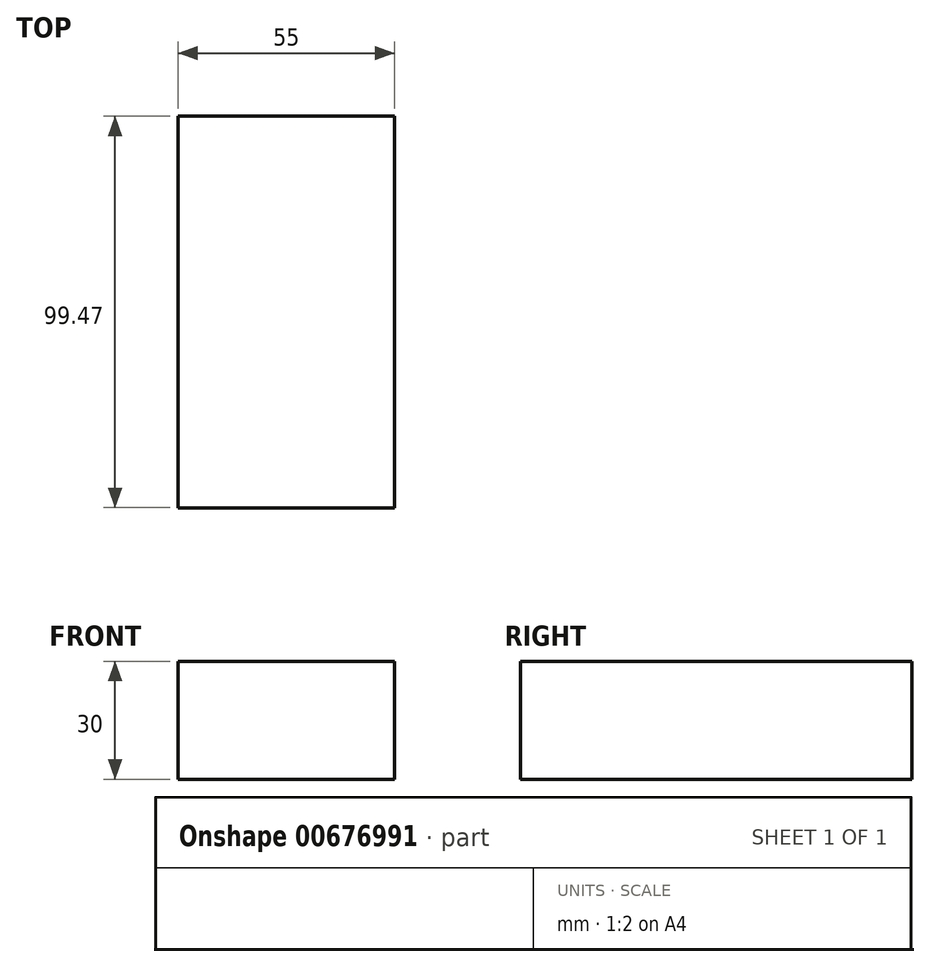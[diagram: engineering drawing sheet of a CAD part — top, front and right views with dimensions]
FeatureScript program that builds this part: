
annotation { "Feature Type Name" : "Feature", "Feature Type Description" : "" }
export const myFeature = defineFeature(function(context is Context, id is Id, definition is map)
    precondition{}
    {
        {
            var Q0;
            Q0=qCreatedBy(makeId("Front.planeOp"),FACE);
            var sketch = newSketch(context, id + "F0", { "sketchPlane" : qUnion([Q0])});
            skLineSegment(sketch, "E0.bottom", {"start": v(-27.5, 15) * mm, "end": v(27.5, 15) * mm});
            skLineSegment(sketch, "E0.top", {"start": v(-27.5, -15) * mm, "end": v(27.5, -15) * mm});
            skLineSegment(sketch, "E0.left", {"start": v(-27.5, 15) * mm, "end": v(-27.5, -15) * mm});
            skLineSegment(sketch, "E0.right", {"start": v(27.5, 15) * mm, "end": v(27.5, -15) * mm});
            skPoint(sketch, "E0.middle", {"position": v(0, 0) * mm});
            skSolve(sketch);
        }
        {
            var Q0;
            Q0 = qSketchRegion(id + "F0", true);
            extrude(context, id + "F1", {"entities" : qUnion([Q0]), "depth" : 30 * mm, "offsetDistance" : 25 * mm});
        }
        {
            var Q0;
            Q0=makeQuery(id+"F1.opExtrude","CAP_FACE",FACE,{"disambiguationData":[OSD([sQuery(id+"F0.wireOp",EDGE,"E0.bottom"),sQuery(id+"F0.wireOp",EDGE,"E0.top"),sQuery(id+"F0.wireOp",EDGE,"E0.left"),sQuery(id+"F0.wireOp",EDGE,"E0.right")])],"isStart":false});
            extrude(context, id + "F2", {"entities" : qUnion([Q0]), "operationType" : NewBodyOperationType.ADD, "endBound" : BoundingType.THROUGH_ALL, "depth" : 25 * mm, "offsetDistance" : 25 * mm});
        }
    });
